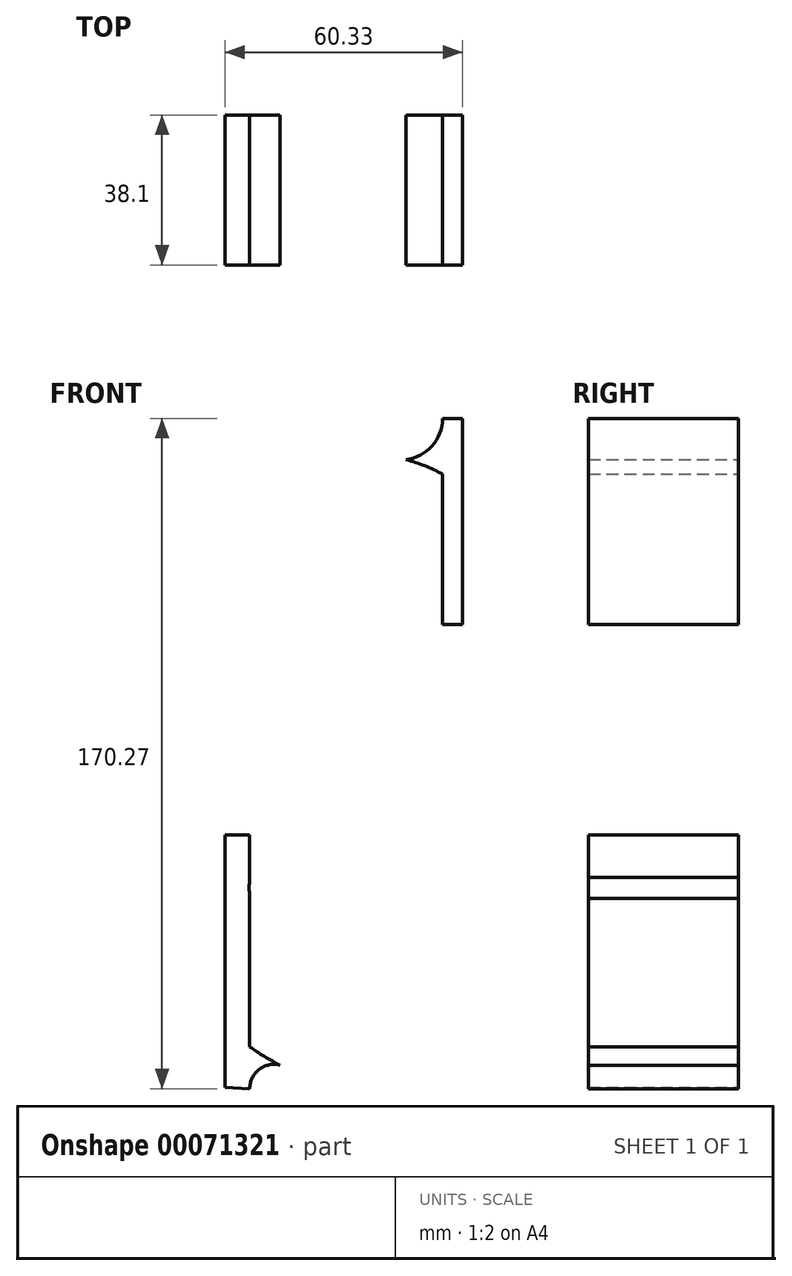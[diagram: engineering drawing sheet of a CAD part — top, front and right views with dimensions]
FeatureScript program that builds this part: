
annotation { "Feature Type Name" : "Feature", "Feature Type Description" : "" }
export const myFeature = defineFeature(function(context is Context, id is Id, definition is map)
    precondition{}
    {
        {
            var Q0;
            Q0=qCreatedBy(makeId("Front.planeOp"),FACE);
            var sketch = newSketch(context, id + "F0", { "sketchPlane" : qUnion([Q0])});
            skArc(sketch, "E0", {"start": v(0, 0) * mm, "mid": v(-15.47, 32.07) * mm, "end": v(19.26, 24.2) * mm});
            skArc(sketch, "E1", {"start": v(0, 0) * mm, "mid": v(47.66, -65.8) * mm, "end": v(-29.72, -90.56) * mm});
            skArc(sketch, "E2", {"start": v(0, -20.32) * mm, "mid": v(-38.83, 29.7) * mm, "end": v(19.26, 54.92) * mm});
            skArc(sketch, "E3", {"start": v(0, -20.32) * mm, "mid": v(20.13, -72.18) * mm, "end": v(-29.72, -47.48) * mm});
            skLineSegment(sketch, "E4", {"start": v(19.26, 16.72) * mm, "end": v(19.26, 69.05) * mm});
            skLineSegment(sketch, "E5", {"start": v(-29.72, -101.22) * mm, "end": v(-29.72, -36.71) * mm});
            skLineSegment(sketch, "E6", {"start": v(19.26, 69.05) * mm, "end": v(24.34, 69.05) * mm});
            skLineSegment(sketch, "E7", {"start": v(24.34, 69.05) * mm, "end": v(24.34, 16.72) * mm});
            skLineSegment(sketch, "E8", {"start": v(24.34, 16.72) * mm, "end": v(19.26, 16.72) * mm});
            skLineSegment(sketch, "E9", {"start": v(-29.72, -36.71) * mm, "end": v(-35.99, -36.71) * mm});
            skLineSegment(sketch, "E10", {"start": v(-35.99, -36.71) * mm, "end": v(-35.99, -100.92) * mm});
            skLineSegment(sketch, "E11", {"start": v(-35.99, -100.92) * mm, "end": v(-29.72, -101.22) * mm});
            skArc(sketch, "E12", {"start": v(9.95, 58.6) * mm, "mid": v(16.6, 62.05) * mm, "end": v(19.26, 69.05) * mm});
            skArc(sketch, "E13", {"start": v(-20.03, -96.14) * mm, "mid": v(-26.4, -95.75) * mm, "end": v(-29.72, -101.22) * mm});
            skSolve(sketch);
        }
        {
            var Q0;
            {var subQ4=sQuery(id+"F0.wireOp",EDGE,"E1");Q0=makeQuery(id+"F0.imprint","IMPRINT",FACE,{"disambiguationData":[TD([[makeQuery(id+"F0.imprint","IMPRINT",EDGE,{"derivedFrom":subQ4}),-1.0]])]});}
            var Q1;
            {var subQ2=sQuery(id+"F0.wireOp",EDGE,"E6");Q1=makeQuery(id+"F0.imprint","IMPRINT",FACE,{"disambiguationData":[TD([[makeQuery(id+"F0.imprint","IMPRINT",EDGE,{"derivedFrom":subQ2}),-1.0]])]});}
            var Q2;
            {var subQ3=sQuery(id+"F0.wireOp",EDGE,"E9");Q2=makeQuery(id+"F0.imprint","IMPRINT",FACE,{"disambiguationData":[TD([[makeQuery(id+"F0.imprint","IMPRINT",EDGE,{"derivedFrom":subQ3}),1.0]])]});}
            var Q3;
            {var subQ0=sQuery(id+"F0.wireOp",EDGE,"E5");var subQ1=sQuery(id+"F0.wireOp",EDGE,"E1");var subQ2=makeQuery(id+"F0.imprint","INTERSECT",VERTEX,{"derivedFrom":[subQ1,subQ0]});Q3=makeQuery(id+"F0.imprint","IMPRINT",FACE,{"disambiguationData":[TD([[makeQuery(id+"F0.imprint","IMPRINT",EDGE,{"disambiguationData":[TD([[subQ2,1.0]])],"derivedFrom":subQ1}),1.0]])]});}
            var Q4;
            {var subQ3=sQuery(id+"F0.wireOp",EDGE,"E12");Q4=makeQuery(id+"F0.imprint","IMPRINT",FACE,{"disambiguationData":[TD([[makeQuery(id+"F0.imprint","IMPRINT",EDGE,{"derivedFrom":subQ3}),-1.0]])]});}
            extrude(context, id + "F1", {"entities" : qUnion([Q0, Q1, Q2, Q3, Q4]), "depth" : 38.1 * mm});
        }
    });
